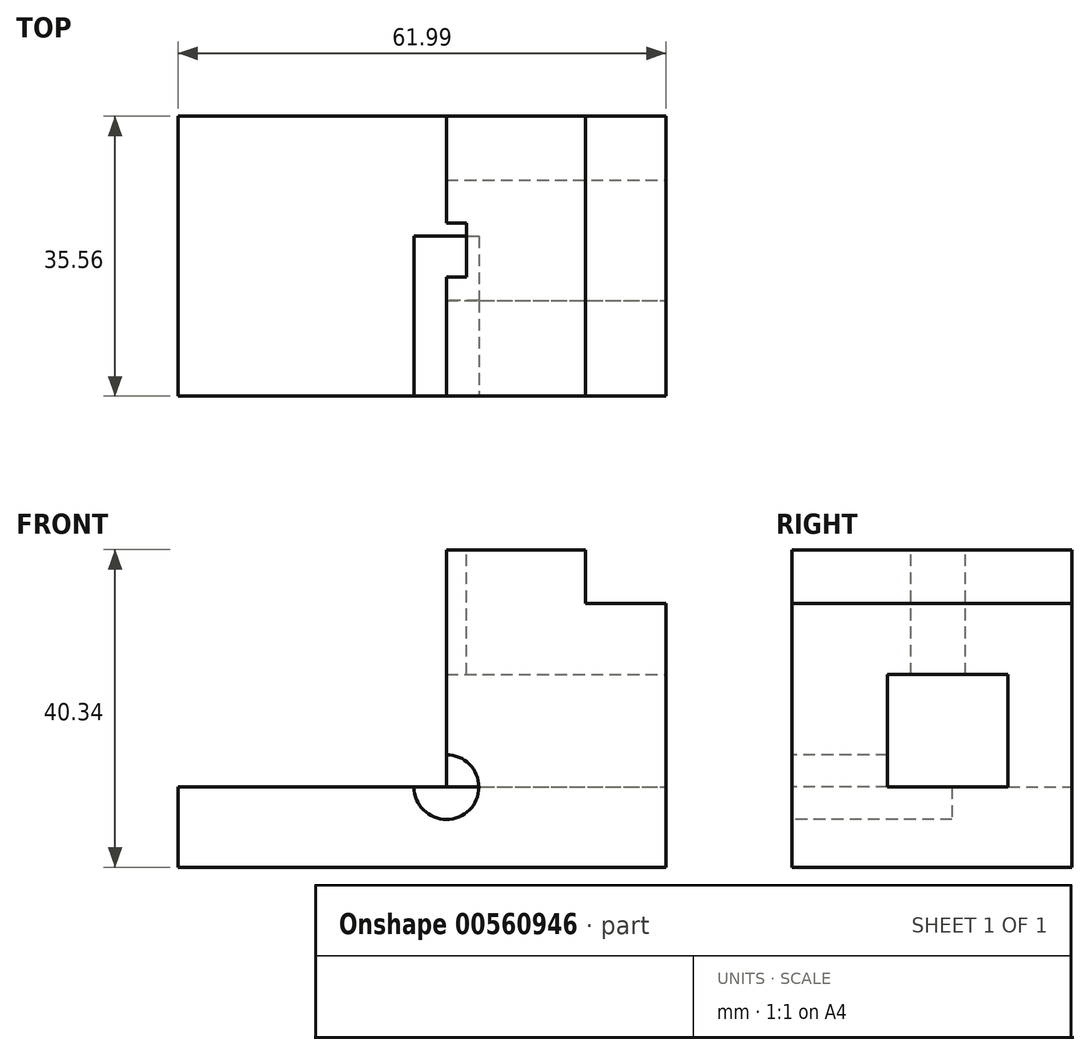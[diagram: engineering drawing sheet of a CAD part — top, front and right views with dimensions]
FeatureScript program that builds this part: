
annotation { "Feature Type Name" : "Feature", "Feature Type Description" : "" }
export const myFeature = defineFeature(function(context is Context, id is Id, definition is map)
    precondition{}
    {
        {
            var Q0;
            Q0=qCreatedBy(makeId("Front.planeOp"),FACE);
            var sketch = newSketch(context, id + "F0", { "sketchPlane" : qUnion([Q0])});
            skLineSegment(sketch, "E0.bottom", {"start": v(27.91, -10.18) * mm, "end": v(-34.08, -10.18) * mm});
            skLineSegment(sketch, "E0.top", {"start": v(27.91, 30.16) * mm, "end": v(-34.08, 30.16) * mm});
            skLineSegment(sketch, "E0.left", {"start": v(27.91, -10.18) * mm, "end": v(27.91, 30.16) * mm});
            skLineSegment(sketch, "E0.right", {"start": v(-34.08, -10.18) * mm, "end": v(-34.08, 30.16) * mm});
            skPoint(sketch, "E0.middle", {"position": v(-3.08, 9.99) * mm});
            skSolve(sketch);
        }
        {
            var Q0;
            Q0=makeQuery(id+"F0.imprint","IMPRINT",FACE,{"disambiguationData":[TD([[makeQuery(id+"F0.imprint","IMPRINT",EDGE,{"derivedFrom":sQuery(id+"F0.wireOp",EDGE,"E0.bottom")}),-1.0]])]});
            extrude(context, id + "F1", {"entities" : qUnion([Q0]), "depth" : 20.32 * mm, "offsetDistance" : 25.4 * mm});
        }
        {
            var Q0;
            Q0=makeQuery(id+"F1.opExtrude","CAP_FACE",FACE,{"disambiguationData":[OSD([sQuery(id+"F0.wireOp",EDGE,"E0.bottom"),sQuery(id+"F0.wireOp",EDGE,"E0.top"),sQuery(id+"F0.wireOp",EDGE,"E0.left"),sQuery(id+"F0.wireOp",EDGE,"E0.right")])],"isStart":false});
            extrude(context, id + "F2", {"entities" : qUnion([Q0]), "operationType" : NewBodyOperationType.ADD, "depth" : 15.24 * mm, "offsetDistance" : 25.4 * mm});
        }
        {
            var Q0;
            Q0=makeQuery(id+"F2.opExtrude","CAP_FACE",FACE,{"disambiguationData":[OSD([sQuery(id+"F0.wireOp",EDGE,"E0.bottom"),sQuery(id+"F0.wireOp",EDGE,"E0.top"),sQuery(id+"F0.wireOp",EDGE,"E0.left"),sQuery(id+"F0.wireOp",EDGE,"E0.right")])],"isStart":false});
            var sketch = newSketch(context, id + "F3", { "sketchPlane" : qUnion([Q0])});
            skCircle(sketch, "E1", {"center": v(0, 0) * mm, "radius": 6.5 * mm});
            skSolve(sketch);
        }
        {
            var Q0;
            Q0=sQuery(id+"F3.wireOp",EDGE,"E1");
            extrude(context, id + "F4", {"bodyType" : ToolBodyType.SURFACE, "surfaceEntities" : qUnion([Q0]), "oppositeDirection" : true, "depth" : 25.4 * mm, "offsetDistance" : 25.4 * mm});
        }
        {
            var Q0;
            Q0=makeQuery(id+"F3.imprint","IMPRINT",FACE,{"disambiguationData":[TD([[makeQuery(id+"F3.imprint","IMPRINT",EDGE,{"derivedFrom":sQuery(id+"F3.wireOp",EDGE,"E1")}),1.0]])]});
            var sketch = newSketch(context, id + "F5", { "sketchPlane" : qUnion([Q0])});
            skCircle(sketch, "E2", {"center": v(0, 0) * mm, "radius": 4.11 * mm});
            skSolve(sketch);
        }
        {
            var Q0;
            Q0 = qSketchRegion(id + "F5", true);
            extrude(context, id + "F6", {"entities" : qUnion([Q0]), "operationType" : NewBodyOperationType.REMOVE, "oppositeDirection" : true, "depth" : 20.32 * mm, "offsetDistance" : 25.4 * mm});
        }
        {
            var Q0;
            {var subQ0=sQuery(id+"F0.wireOp",EDGE,"E0.top");Q0=makeQuery(id+"F2.boolean.opBoolean","MERGE",FACE,{"derivedFrom":[makeQuery(id+"F1.opExtrude","SWEPT_FACE",FACE,{"disambiguationData":[OSD([subQ0])]}),makeQuery(id+"F2.opExtrude","SWEPT_FACE",FACE,{"disambiguationData":[OSD([subQ0])]})]});}
            var sketch = newSketch(context, id + "F7", { "sketchPlane" : qUnion([Q0])});
            skLineSegment(sketch, "E3.bottom", {"start": v(-11.48, -13.54) * mm, "end": v(2.52, -13.54) * mm});
            skLineSegment(sketch, "E3.top", {"start": v(-11.48, -20.45) * mm, "end": v(2.52, -20.45) * mm});
            skLineSegment(sketch, "E3.left", {"start": v(-11.48, -13.54) * mm, "end": v(-11.48, -20.45) * mm});
            skLineSegment(sketch, "E3.right", {"start": v(2.52, -13.54) * mm, "end": v(2.52, -20.45) * mm});
            skSolve(sketch);
        }
        {
            var Q0;
            Q0=makeQuery(id+"F7.imprint","IMPRINT",FACE,{"disambiguationData":[TD([[makeQuery(id+"F7.imprint","IMPRINT",EDGE,{"derivedFrom":sQuery(id+"F7.wireOp",EDGE,"E3.bottom")}),-1.0]])]});
            extrude(context, id + "F8", {"entities" : qUnion([Q0]), "operationType" : NewBodyOperationType.REMOVE, "oppositeDirection" : true, "depth" : 17.78 * mm, "offsetDistance" : 25.4 * mm});
        }
        {
            var Q0;
            {var subQ0=sQuery(id+"F0.wireOp",EDGE,"E0.left");Q0=makeQuery(id+"F2.boolean.opBoolean","MERGE",FACE,{"derivedFrom":[makeQuery(id+"F1.opExtrude","SWEPT_FACE",FACE,{"disambiguationData":[OSD([subQ0])]}),makeQuery(id+"F2.opExtrude","SWEPT_FACE",FACE,{"disambiguationData":[OSD([subQ0])]})]});}
            var sketch = newSketch(context, id + "F9", { "sketchPlane" : qUnion([Q0])});
            skLineSegment(sketch, "E4.bottom", {"start": v(-23.43, 14.28) * mm, "end": v(-8.12, 14.28) * mm});
            skLineSegment(sketch, "E4.top", {"start": v(-23.43, 0) * mm, "end": v(-8.12, 0) * mm});
            skLineSegment(sketch, "E4.left", {"start": v(-23.43, 14.28) * mm, "end": v(-23.43, 0) * mm});
            skLineSegment(sketch, "E4.right", {"start": v(-8.12, 14.28) * mm, "end": v(-8.12, 0) * mm});
            skSolve(sketch);
        }
        {
            var Q0;
            Q0 = qSketchRegion(id + "F9", true);
            extrude(context, id + "F10", {"entities" : qUnion([Q0]), "operationType" : NewBodyOperationType.REMOVE, "endBound" : BoundingType.THROUGH_ALL, "oppositeDirection" : true, "depth" : 25.4 * mm, "offsetDistance" : 25.4 * mm, "hasSecondDirection" : true, "secondDirectionOppositeDirection" : false, "secondDirectionDepth" : 25.4 * mm});
        }
        {
            var Q0;
            Q0=makeQuery(id+"F3.imprint","IMPRINT",FACE,{"disambiguationData":[TD([[makeQuery(id+"F3.imprint","IMPRINT",EDGE,{"derivedFrom":sQuery(id+"F3.wireOp",EDGE,"E1")}),-1.0]])]});
            var sketch = newSketch(context, id + "F11", { "sketchPlane" : qUnion([Q0])});
            skLineSegment(sketch, "E5.bottom", {"start": v(17.68, 31.83) * mm, "end": v(29.68, 31.83) * mm});
            skLineSegment(sketch, "E5.top", {"start": v(17.68, 23.33) * mm, "end": v(29.68, 23.33) * mm});
            skLineSegment(sketch, "E5.left", {"start": v(17.68, 31.83) * mm, "end": v(17.68, 23.33) * mm});
            skLineSegment(sketch, "E5.right", {"start": v(29.68, 31.83) * mm, "end": v(29.68, 23.33) * mm});
            skSolve(sketch);
        }
        {
            var Q0;
            {var subQ0=sQuery(id+"F11.wireOp",EDGE,"E5.left");var subQ1=sQuery(id+"F11.wireOp",EDGE,"E5.top");var subQ2=makeQuery(id+"F11.imprint","INTERSECT",VERTEX,{"derivedFrom":[subQ1,subQ0]});Q0=makeQuery(id+"F11.imprint","IMPRINT",FACE,{"disambiguationData":[TD([[makeQuery(id+"F11.imprint","IMPRINT",EDGE,{"disambiguationData":[TD([[subQ2,-1.0]])],"derivedFrom":subQ1}),1.0]])]});}
            extrude(context, id + "F12", {"entities" : qUnion([Q0]), "operationType" : NewBodyOperationType.REMOVE, "endBound" : BoundingType.THROUGH_ALL, "oppositeDirection" : true, "depth" : 25 * mm, "offsetDistance" : 25 * mm});
        }
        {
            var Q0;
            Q0=makeQuery(id+"F0.imprint","IMPRINT",FACE,{"disambiguationData":[TD([[makeQuery(id+"F0.imprint","IMPRINT",EDGE,{"derivedFrom":sQuery(id+"F0.wireOp",EDGE,"E0.bottom")}),-1.0]])]});
            var sketch = newSketch(context, id + "F13", { "sketchPlane" : qUnion([Q0])});
            skLineSegment(sketch, "E6.bottom", {"start": v(-38, 35) * mm, "end": v(0, 35) * mm});
            skLineSegment(sketch, "E6.top", {"start": v(-38, 0) * mm, "end": v(0, 0) * mm});
            skLineSegment(sketch, "E6.left", {"start": v(-38, 35) * mm, "end": v(-38, 0) * mm});
            skLineSegment(sketch, "E6.right", {"start": v(0, 35) * mm, "end": v(0, 0) * mm});
            skSolve(sketch);
        }
        {
            var Q0;
            {var subQ0=sQuery(id+"F13.wireOp",EDGE,"E6.right");var subQ1=sQuery(id+"F13.wireOp",EDGE,"E6.top");var subQ2=makeQuery(id+"F13.imprint","INTERSECT",VERTEX,{"derivedFrom":[subQ1,subQ0]});Q0=makeQuery(id+"F13.imprint","IMPRINT",FACE,{"disambiguationData":[TD([[makeQuery(id+"F13.imprint","IMPRINT",EDGE,{"disambiguationData":[TD([[subQ2,1.0]])],"derivedFrom":subQ1}),1.0]])]});}
            extrude(context, id + "F14", {"entities" : qUnion([Q0]), "operationType" : NewBodyOperationType.REMOVE, "endBound" : BoundingType.THROUGH_ALL, "depth" : 25 * mm, "offsetDistance" : 25 * mm});
        }
    });
